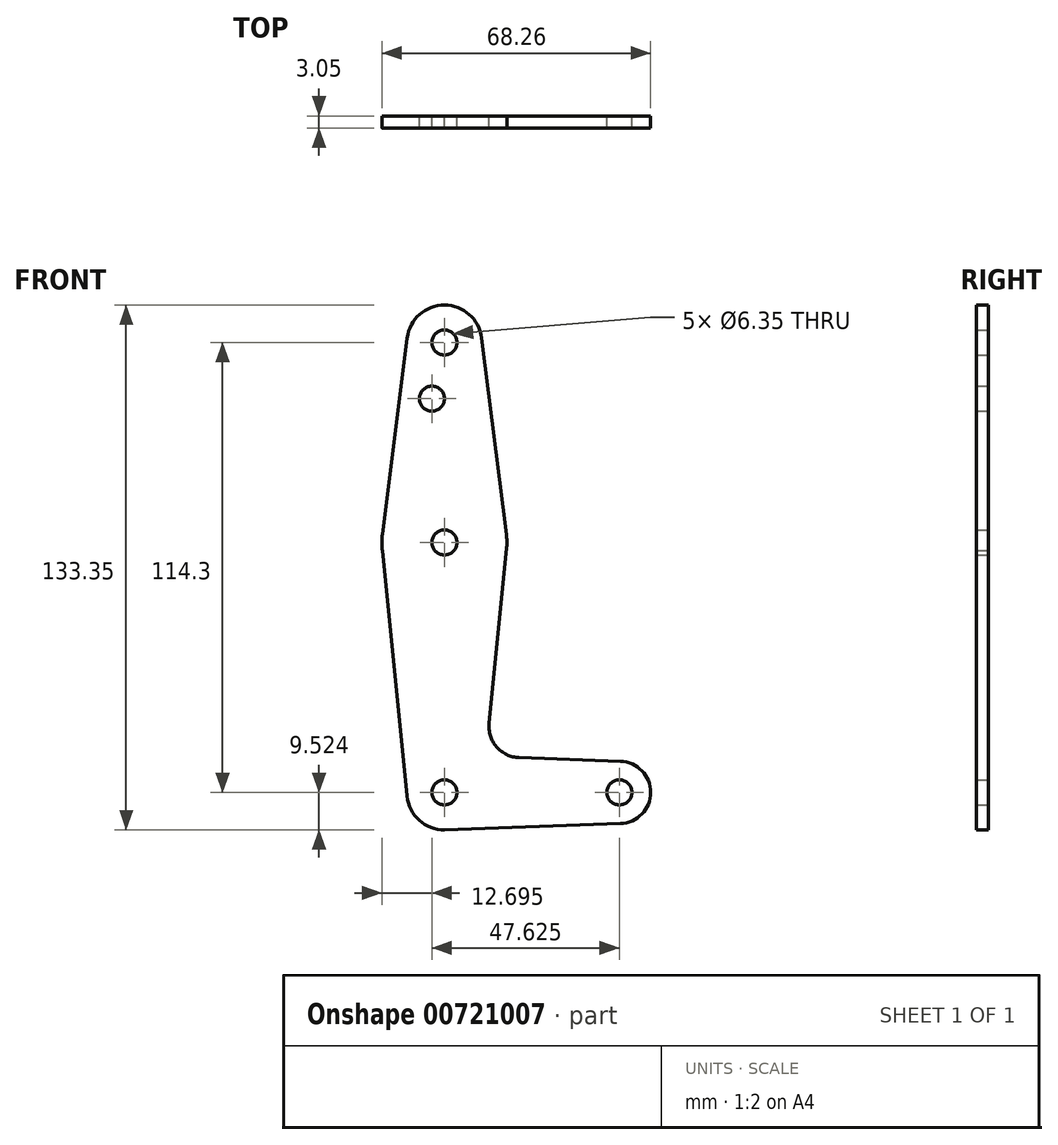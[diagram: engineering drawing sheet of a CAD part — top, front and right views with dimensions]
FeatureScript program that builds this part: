
annotation { "Feature Type Name" : "Feature", "Feature Type Description" : "" }
export const myFeature = defineFeature(function(context is Context, id is Id, definition is map)
    precondition{}
    {
        {
            var Q0;
            Q0=qCreatedBy(makeId("Front.planeOp"),FACE);
            var sketch = newSketch(context, id + "F0", { "sketchPlane" : qUnion([Q0])});
            skCircle(sketch, "E0", {"center": v(-38.04, -54.95) * mm, "radius": 9.53 * mm});
            skLineSegment(sketch, "E1", {"start": v(-38.04, -54.95) * mm, "end": v(6.41, -54.95) * mm, "construction": true});
            skLineSegment(sketch, "E2", {"start": v(-38.04, -54.95) * mm, "end": v(-38.04, 59.35) * mm, "construction": true});
            skCircle(sketch, "E3", {"center": v(-38.04, 59.35) * mm, "radius": 9.53 * mm});
            skCircle(sketch, "E4", {"center": v(-38.04, 8.55) * mm, "radius": 15.88 * mm});
            skCircle(sketch, "E5", {"center": v(6.41, -54.95) * mm, "radius": 7.94 * mm});
            skLineSegment(sketch, "E6", {"start": v(-38.04, 8.55) * mm, "end": v(-38.04, -54.95) * mm, "construction": true});
            skLineSegment(sketch, "E7", {"start": v(-47.49, 60.54) * mm, "end": v(-53.79, 10.54) * mm});
            skLineSegment(sketch, "E8", {"start": v(-53.79, 10.54) * mm, "end": v(-53.79, 6.57) * mm});
            skLineSegment(sketch, "E9", {"start": v(-53.79, 6.57) * mm, "end": v(-47.52, -55.9) * mm});
            skLineSegment(sketch, "E10", {"start": v(-28.59, 60.54) * mm, "end": v(-22.29, 10.54) * mm});
            skLineSegment(sketch, "E11", {"start": v(-22.24, 6.97) * mm, "end": v(-26.7, -37.36) * mm});
            skLineSegment(sketch, "E12", {"start": v(-19.07, -46.1) * mm, "end": v(6.7, -47.01) * mm});
            skCircle(sketch, "E13", {"center": v(-38.04, 8.55) * mm, "radius": 3.18 * mm});
            skCircle(sketch, "E14", {"center": v(-41.21, 45.08) * mm, "radius": 3.18 * mm});
            skCircle(sketch, "E15", {"center": v(-38.04, -54.95) * mm, "radius": 3.18 * mm});
            skCircle(sketch, "E16", {"center": v(6.41, -54.95) * mm, "radius": 3.18 * mm});
            skCircle(sketch, "E17", {"center": v(-38.04, 59.35) * mm, "radius": 3.18 * mm});
            skLineSegment(sketch, "E18", {"start": v(-38, -64.47) * mm, "end": v(6.7, -62.88) * mm});
            skArc(sketch, "E19.filletArc", {"start": v(-26.7, -37.36) * mm, "mid": v(-24.78, -43.38) * mm, "end": v(-19.07, -46.1) * mm});
            skSolve(sketch);
        }
        {
            var Q0;
            {var subQ0=sQuery(id+"F0.wireOp",EDGE,"E18");var subQ1=sQuery(id+"F0.wireOp",EDGE,"E0");var subQ2=makeQuery(id+"F0.imprint","INTERSECT",VERTEX,{"disambiguationData":[OD(0.0)],"derivedFrom":[subQ1,subQ0]});Q0=makeQuery(id+"F0.imprint","IMPRINT",FACE,{"disambiguationData":[TD([[makeQuery(id+"F0.imprint","IMPRINT",EDGE,{"disambiguationData":[TD([[subQ2,-1.0]])],"derivedFrom":subQ1}),1.0]])]});}
            var Q1;
            {var subQ0=sQuery(id+"F0.wireOp",EDGE,"E8");Q1=makeQuery(id+"F0.imprint","IMPRINT",FACE,{"disambiguationData":[TD([[makeQuery(id+"F0.imprint","IMPRINT",EDGE,{"derivedFrom":subQ0}),-1.0]])]});}
            var Q2;
            Q2=makeQuery(id+"F0.imprint","IMPRINT",FACE,{"disambiguationData":[TD([[makeQuery(id+"F0.imprint","IMPRINT",EDGE,{"derivedFrom":sQuery(id+"F0.wireOp",EDGE,"E17")}),-1.0]])]});
            var Q3;
            Q3=makeQuery(id+"F0.imprint","IMPRINT",FACE,{"disambiguationData":[TD([[makeQuery(id+"F0.imprint","IMPRINT",EDGE,{"derivedFrom":sQuery(id+"F0.wireOp",EDGE,"E16")}),-1.0]])]});
            var Q4;
            Q4=makeQuery(id+"F0.imprint","IMPRINT",FACE,{"disambiguationData":[TD([[makeQuery(id+"F0.imprint","IMPRINT",EDGE,{"derivedFrom":sQuery(id+"F0.wireOp",EDGE,"E15")}),-1.0]])]});
            var Q5;
            {var subQ0=sQuery(id+"F0.wireOp",EDGE,"E9");Q5=makeQuery(id+"F0.imprint","IMPRINT",FACE,{"disambiguationData":[TD([[makeQuery(id+"F0.imprint","IMPRINT",EDGE,{"derivedFrom":subQ0}),1.0]])]});}
            var Q6;
            {var subQ3=sQuery(id+"F0.wireOp",EDGE,"E8");Q6=makeQuery(id+"F0.imprint","IMPRINT",FACE,{"disambiguationData":[TD([[makeQuery(id+"F0.imprint","IMPRINT",EDGE,{"derivedFrom":subQ3}),1.0]])]});}
            var Q7;
            {var subQ0=sQuery(id+"F0.wireOp",EDGE,"E7");Q7=makeQuery(id+"F0.imprint","IMPRINT",FACE,{"disambiguationData":[TD([[makeQuery(id+"F0.imprint","IMPRINT",EDGE,{"derivedFrom":subQ0}),1.0]])]});}
            extrude(context, id + "F1", {"entities" : qUnion([Q0, Q1, Q2, Q3, Q4, Q5, Q6, Q7]), "depth" : 3.05 * mm, "offsetDistance" : 25.4 * mm});
        }
    });
